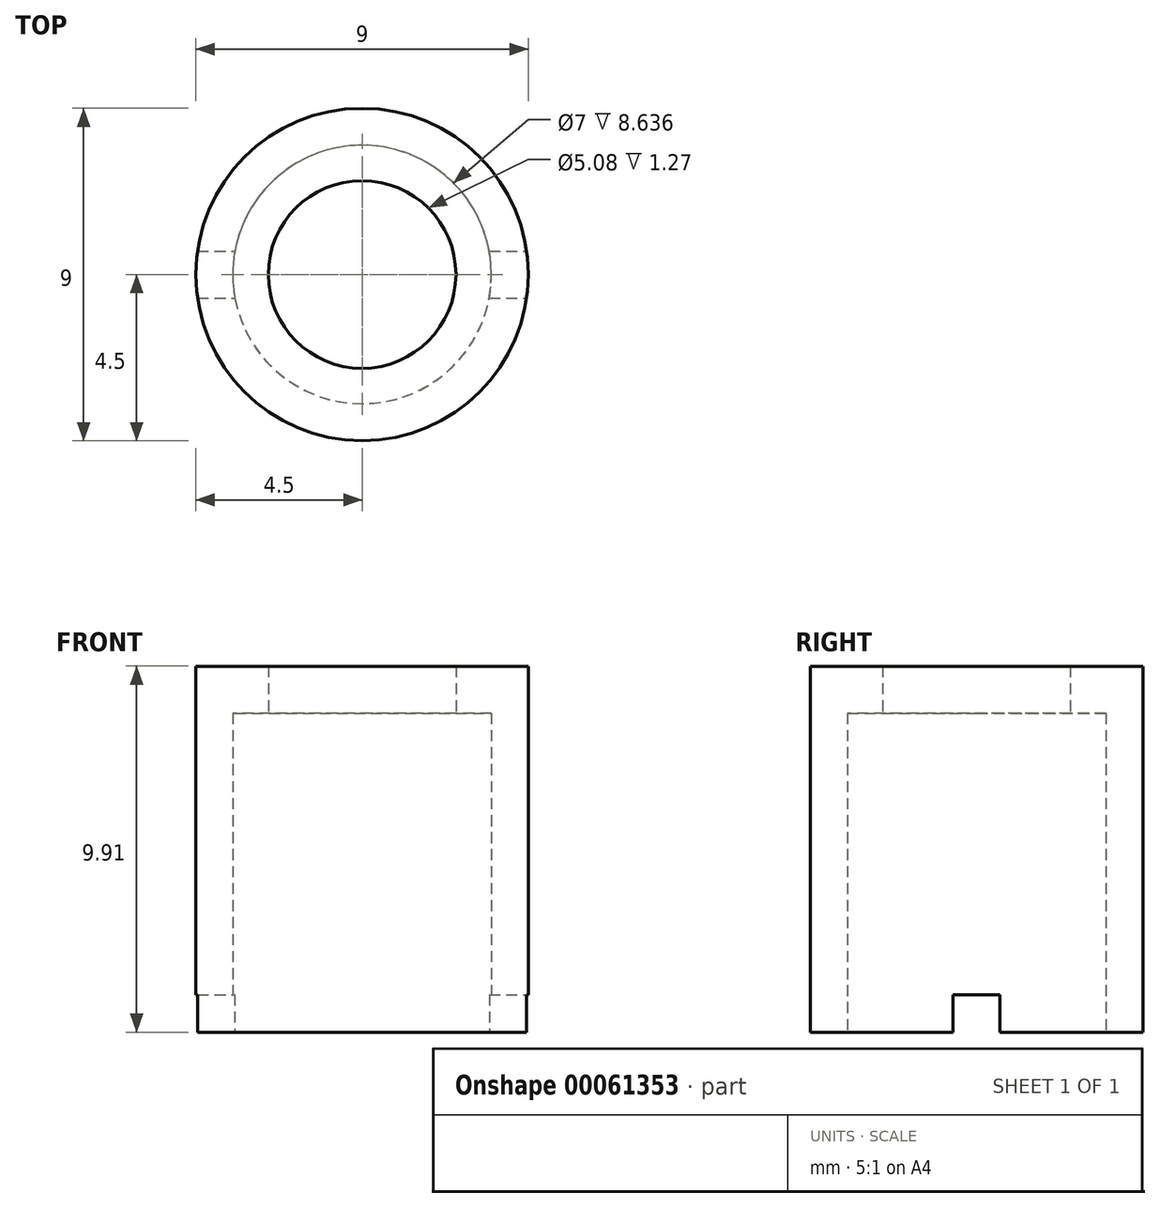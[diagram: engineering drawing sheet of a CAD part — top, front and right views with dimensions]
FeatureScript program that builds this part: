
annotation { "Feature Type Name" : "Feature", "Feature Type Description" : "" }
export const myFeature = defineFeature(function(context is Context, id is Id, definition is map)
    precondition{}
    {
        {
            var Q0;
            Q0=qCreatedBy(makeId("Top.planeOp"),FACE);
            var sketch = newSketch(context, id + "F0", { "sketchPlane" : qUnion([Q0])});
            skCircle(sketch, "E0", {"center": v(0, 0) * mm, "radius": 4.5 * mm});
            skCircle(sketch, "E1", {"center": v(0, 0) * mm, "radius": 3.5 * mm});
            skSolve(sketch);
        }
        {
            var Q0;
            Q0 = qSketchRegion(id + "F0", true);
            extrude(context, id + "F1", {"entities" : qUnion([Q0]), "depth" : 8.64 * mm});
        }
        {
            var Q0;
            Q0=qCreatedBy(makeId("Top.planeOp"),FACE);
            var sketch = newSketch(context, id + "F2", { "sketchPlane" : qUnion([Q0])});
            skLineSegment(sketch, "E2.rect.bottom", {"start": v(-5.08, 0.63) * mm, "end": v(5.08, 0.63) * mm});
            skLineSegment(sketch, "E2.rect.top", {"start": v(-5.08, -0.64) * mm, "end": v(5.08, -0.64) * mm});
            skLineSegment(sketch, "E2.rect.left", {"start": v(-5.08, 0.63) * mm, "end": v(-5.08, -0.64) * mm});
            skLineSegment(sketch, "E2.rect.right", {"start": v(5.08, 0.64) * mm, "end": v(5.08, -0.64) * mm});
            skPoint(sketch, "E2.rect.middle", {"position": v(0, 0) * mm});
            skSolve(sketch);
        }
        {
            var Q0;
            Q0 = qSketchRegion(id + "F2", true);
            extrude(context, id + "F3", {"entities" : qUnion([Q0]), "operationType" : NewBodyOperationType.REMOVE, "depth" : 1.02 * mm});
        }
        {
            var Q0;
            Q0=makeQuery(id+"F1.opExtrude","CAP_FACE",FACE,{"disambiguationData":[OSD([sQuery(id+"F0.wireOp",EDGE,"E0"),sQuery(id+"F0.wireOp",EDGE,"E1")])],"isStart":false});
            var sketch = newSketch(context, id + "F4", { "sketchPlane" : qUnion([Q0])});
            skCircle(sketch, "E3", {"center": v(0, 0) * mm, "radius": 4.5 * mm});
            skCircle(sketch, "E4", {"center": v(0, 0) * mm, "radius": 2.54 * mm});
            skSolve(sketch);
        }
        {
            var Q0;
            Q0 = qSketchRegion(id + "F4", true);
            extrude(context, id + "F5", {"entities" : qUnion([Q0]), "operationType" : NewBodyOperationType.ADD, "depth" : 1.27 * mm});
        }
    });
